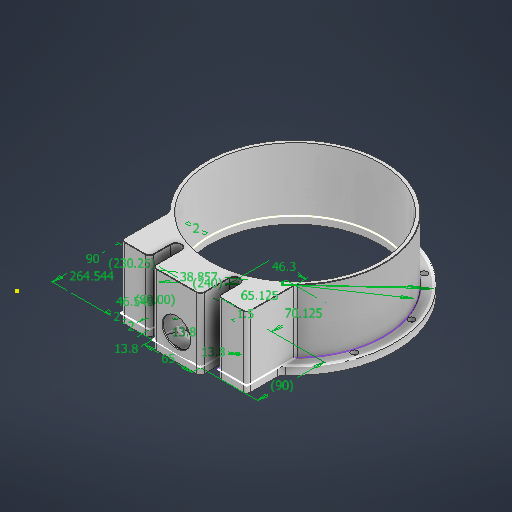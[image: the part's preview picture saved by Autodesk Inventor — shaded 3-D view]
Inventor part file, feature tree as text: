
AUTODESK INVENTOR PART (.ipt)
format: ipt  version: 2025 (Build 290162000, 162)  size: 691,712 bytes
history: native  units: in
note: dims shown in document units (in); Inventor stores cm internally (conversion verified against a paired STEP export)
features: extrude x20, sketch x14, fillet x9, other x3, chamfer x2, plane x1
ambient origin geometry x8: Origin, YZ Plane, XZ Plane, XY Plane, X Axis, Y Axis, Z Axis, Center Point
bodies: Body1 (feature_tree)
feature tree (49):
  other  "Cylinder.ipt"
  extrude  "Extrusion1"  Depth=0.3937in
  extrude  "Extrusion2"  Depth=0.3937in TaperAngle=0.0deg
  sketch  "Sketch3"  dims[d7=11.2205in d8=10.6299in]
  extrude  "Extrusion3"  Depth=10.6299in
  extrude  "Extrusion5"  Depth=0.1969in TaperAngle=0.0deg
  sketch  "Sketch6"  dims[d24=0.1969in d25=0.0in d31=0.0in d32=0.0in]
  extrude  "Extrusion6"  Depth=0.2953in
  extrude  "Extrusion7"  TaperAngle=0.0deg  [1 undecoded]
  extrude  "Extrusion8"  Depth=9.8425in
  plane  "Work Plane1"
  extrude  "Extrusion9"  Depth=9.065in
  extrude  "Extrusion21"  Depth=0.3937in
  sketch  "Sketch18"  dims[d107=2.2047in d108=0.0in d111=3.937in d112=0.0in]
  extrude  "Extrusion22"  Depth=3.937in TaperAngle=0.0deg
  sketch  "Sketch19"  dims[d113=2.5591in d115=2.2047in d116=0.0in]
  extrude  "Extrusion23"  Depth=2.2047in TaperAngle=0.0deg
  extrude  "Extrusion27"  Depth=0.5433in
  extrude  "Extrusion31"  Depth=9.4488in
  extrude  "Extrusion32"  Depth=0.3937in TaperAngle=0.0deg
  extrude  "Extrusion33"  TaperAngle=0.0deg  [1 undecoded]
  extrude  "Extrusion34"  Depth=0.3937in
  fillet  "Fillet9"  Radius=0.0787in
  fillet  "Fillet10"  Radius=1.8325in
  fillet  "Fillet11"  [1 undecoded]
  fillet  "Fillet12"  Radius=2.2047in
  chamfer  "Chamfer5"  Distance=4.1339in
  extrude  "Extrusion36"  Depth=0.3937in TaperAngle=0.0deg
  fillet  "Fillet13"  Radius=0.0787in
  chamfer  "Chamfer6"  Distance=0.3937in
  fillet  "Fillet15"  Radius=0.0787in
  fillet  "Fillet16"  Radius=0.1969in
  fillet  "Fillet17"  Radius=0.1969in
  fillet  "Fillet18"  Radius=0.0197in
  extrude  "Extrusion38"  Depth=0.3937in TaperAngle=0.0deg
  extrude  "Extrusion39"  Depth=0.1969in
  extrude  "Extrusion40"  Depth=0.3937in TaperAngle=45.0deg
  other  "Solid12::Cylinder.ipt"
  other  "TaggingFeature1"
  sketch  "Sketch1"  dims[d0=0.3937in d2=10.2362in]
  sketch  "Sketch2"  dims[d3=0.0in d4=0.0in d5=0.3937in d6=0.0in]
  sketch  "Sketch5"  dims[d17=10.6299in d18=0.2953in]
  sketch  "Sketch7"  dims[d33=2.1654in d34=0.0in d35=9.8425in]
  sketch  "Sketch9"  dims[d36=10.6299in d46=9.065in]
  sketch  "Sketch14"  dims[d47=0.3937in d48=0.0in d88=0.0787in]
  sketch  "Sketch22"  dims[d117=0.0591in d119=0.5433in]
  sketch  "Sketch24"  dims[d120=0.5433in d122=9.4488in]
  sketch  "Sketch Circular Pattern3"  dims[d10=0.1969in d11=0.0in d15=0.1969in d16=0.0in]
  sketch  "Sketch26"  dims[d134=0.0787in d141=0.3937in d142=0.0in d159=0.0in d160=0.0in d164=1.5298in d165=0.0787in d166=1.8325in d167=90.0deg d169=2.2047in d170=0.0in d171=4.1339in d172=0.0in d173=1.1614in d174=0.0in d175=0.0787in d177=0.3937in d178=0.0787in d179=0.1969in d180=0.1969in d184=0.0197in d185=0.0787in d186=45.0deg d189=1.9291in d190=0.0in d193=0.1969in d195=0.3912in d196=1.2662in d197=45.0deg d198=0.1969in d199=0.1969in d200=0.1969in d206=0.3937in d207=1.5157in d208=1.378in d209=0.2165in d210=0.3425in d211=3.937in d213=360.0deg d215=0.1181in d216=0.0in d217=10.4151in d218=9.065in d219=6.1806in d220=0.0in d221=0.3937in d222=0.0in d223=0.5433in d224=1.8228in d225=3.5433in d226=2.564in d227=2.7608in d228=3.5433in d143=0.0197in d144=0.0344in d145=0.0197in d146=0.0344in d153=0.0in d154=0.0in d155=0.0in d156=0.0in d201=0.0197in d202=0.0344in d203=0.0197in d204=0.0344in]
note: 3 required parameter values undecoded (feature->parameter linkage not recoverable at this tier; creation-order binding heuristic only, values carry confidence <= 0.55)
